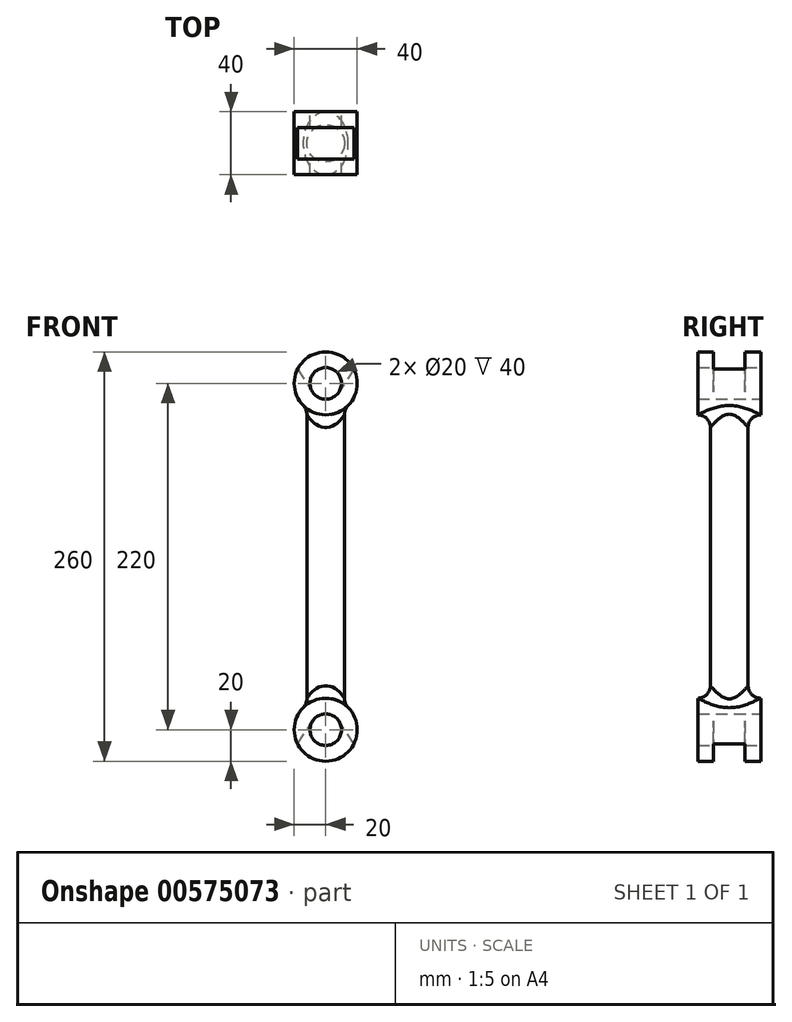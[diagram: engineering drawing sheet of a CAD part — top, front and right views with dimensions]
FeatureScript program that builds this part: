
annotation { "Feature Type Name" : "Feature", "Feature Type Description" : "" }
export const myFeature = defineFeature(function(context is Context, id is Id, definition is map)
    precondition{}
    {
        {
            var Q0;
            Q0=qCreatedBy(makeId("Front.planeOp"),FACE);
            var sketch = newSketch(context, id + "F0", { "sketchPlane" : qUnion([Q0])});
            skCircle(sketch, "E0", {"center": v(0, 0) * mm, "radius": 20 * mm});
            skCircle(sketch, "E1", {"center": v(0, 0) * mm, "radius": 10 * mm});
            skPoint(sketch, "E2.end.orphan", {"position": v(19.32, -5.17) * mm});
            skPoint(sketch, "E3.end.orphan", {"position": v(10, -40) * mm});
            skPoint(sketch, "E3.start.orphan", {"position": v(0, -40) * mm});
            skPoint(sketch, "E4.MirrorCS.end.orphan", {"position": v(-10, -40) * mm});
            skPoint(sketch, "E5.MirrorCS.end.orphan", {"position": v(-19.32, -5.17) * mm});
            skSolve(sketch);
        }
        {
            var Q0;
            Q0=makeQuery(id+"F0.imprint","IMPRINT",FACE,{"disambiguationData":[TD([[makeQuery(id+"F0.imprint","IMPRINT",EDGE,{"derivedFrom":sQuery(id+"F0.wireOp",EDGE,"E0")}),1.0]])]});
            extrude(context, id + "F1", {"entities" : qUnion([Q0]), "depth" : 40 * mm, "offsetDistance" : 25 * mm, "symmetric" : true});
        }
        {
            var Q0;
            Q0=qCreatedBy(makeId("Front.planeOp"),FACE);
            var sketch = newSketch(context, id + "F2", { "sketchPlane" : qUnion([Q0])});
            skArc(sketch, "E6", {"start": v(-8.35, -5.5) * mm, "mid": v(0, -10) * mm, "end": v(8.35, -5.5) * mm});
            skLineSegment(sketch, "E7", {"start": v(-35, 35) * mm, "end": v(-8.35, -5.5) * mm});
            skLineSegment(sketch, "E8.MirrorCS", {"start": v(35, 35) * mm, "end": v(8.35, -5.5) * mm});
            skLineSegment(sketch, "E9", {"start": v(-35, 35) * mm, "end": v(35, 35) * mm});
            skSolve(sketch);
        }
        {
            var Q0;
            Q0=makeQuery(id+"F2.imprint","IMPRINT",FACE,{"disambiguationData":[TD([[makeQuery(id+"F2.imprint","IMPRINT",EDGE,{"derivedFrom":sQuery(id+"F2.wireOp",EDGE,"E6")}),1.0]])]});
            extrude(context, id + "F3", {"entities" : qUnion([Q0]), "operationType" : NewBodyOperationType.REMOVE, "oppositeDirection" : true, "depth" : 20 * mm, "offsetDistance" : 25 * mm, "symmetric" : true});
        }
        {
            var Q0;
            Q0=qCreatedBy(makeId("Top.planeOp"),FACE);
            cPlane(context, id + "F4", {"entities" : qUnion([Q0]), "cplaneType" : CPlaneType.OFFSET, "offset" : 10 * mm, "oppositeDirection" : true, "width" : 150 * mm, "height" : 150 * mm});
        }
        {
            var Q0;
            Q0=qCreatedBy(id+"F4.planeOp",FACE);
            var sketch = newSketch(context, id + "F5", { "sketchPlane" : qUnion([Q0])});
            skCircle(sketch, "E10", {"center": v(0, 0) * mm, "radius": 12 * mm});
            skSolve(sketch);
        }
        {
            var Q0;
            Q0 = qSketchRegion(id + "F5", true);
            extrude(context, id + "F6", {"entities" : qUnion([Q0]), "operationType" : NewBodyOperationType.ADD, "oppositeDirection" : true, "depth" : 100 * mm, "offsetDistance" : 25 * mm});
        }
        {
            var Q0;
            Q0=makeQuery(id+"F6.boolean.opBoolean","INTERSECT",EDGE,{"derivedFrom":[makeQuery(id+"F1.opExtrude","SWEPT_FACE",FACE,{"disambiguationData":[OSD([sQuery(id+"F0.wireOp",EDGE,"E0")])]}),makeQuery(id+"F6.opExtrude","SWEPT_FACE",FACE,{"disambiguationData":[OSD([sQuery(id+"F5.wireOp",EDGE,"E10")])]})]});
            fillet(context, id + "F7", {"entities" : qUnion([Q0]), "radius" : 8 * mm, "tangentPropagation" : true, "allowEdgeOverflow" : false});
        }
        {
            var Q0;
            Q0=makeQuery(id+"F1.opExtrude","SWEPT_BODY",BODY,{"disambiguationData":[OSD([sQuery(id+"F0.wireOp",EDGE,"E0"),sQuery(id+"F0.wireOp",EDGE,"E1")])]});
            var Q1;
            Q1=makeQuery(id+"F6.opExtrude","CAP_FACE",FACE,{"disambiguationData":[OSD([sQuery(id+"F5.wireOp",EDGE,"E10")])],"isStart":false});
            mirror(context, id + "F8", {"operationType" : NewBodyOperationType.ADD, "entities" : qUnion([Q0]), "mirrorPlane" : qUnion([Q1])});
        }
    });
